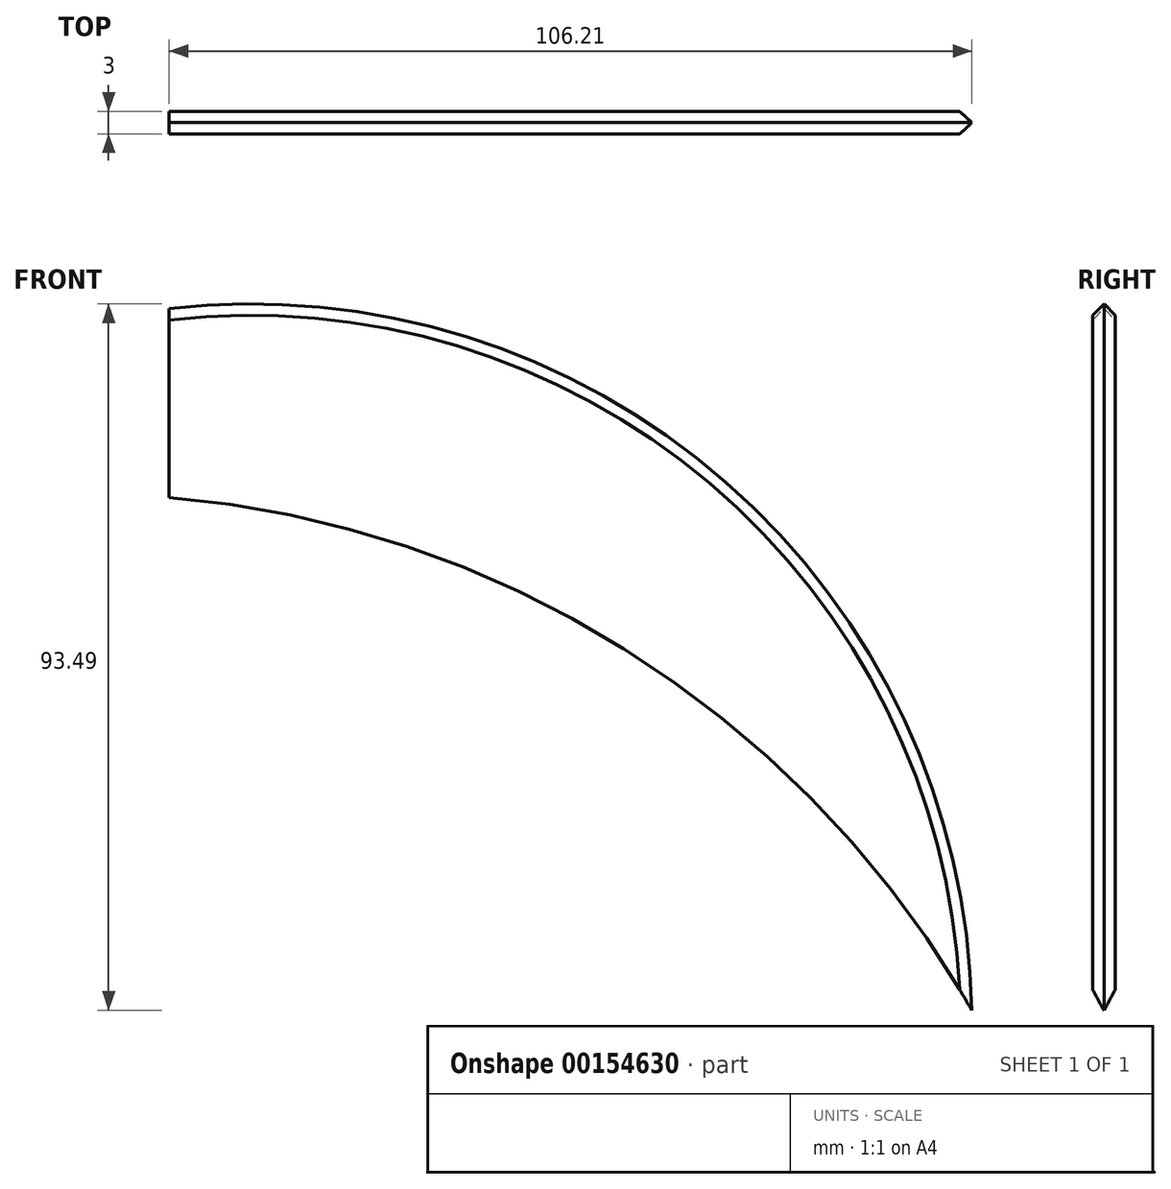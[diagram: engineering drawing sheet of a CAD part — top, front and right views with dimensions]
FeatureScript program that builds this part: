
annotation { "Feature Type Name" : "Feature", "Feature Type Description" : "" }
export const myFeature = defineFeature(function(context is Context, id is Id, definition is map)
    precondition{}
    {
        {
            var Q0;
            Q0=qCreatedBy(makeId("Front.planeOp"),FACE);
            var sketch = newSketch(context, id + "F0", { "sketchPlane" : qUnion([Q0])});
            skArc(sketch, "E0", {"start": v(106.2, -67.87) * mm, "mid": v(61.48, -20.83) * mm, "end": v(0, 0) * mm});
            skLineSegment(sketch, "E1", {"start": v(0, 0) * mm, "end": v(0, 25) * mm});
            skArc(sketch, "E2", {"start": v(106.2, -67.87) * mm, "mid": v(73.64, 2.05) * mm, "end": v(0, 25) * mm});
            skSolve(sketch);
        }
        {
            var Q0;
            Q0=makeQuery(id+"F0.imprint","IMPRINT",FACE,{"disambiguationData":[TD([[makeQuery(id+"F0.imprint","IMPRINT",EDGE,{"derivedFrom":sQuery(id+"F0.wireOp",EDGE,"E0")}),-1.0]])]});
            extrude(context, id + "F1", {"entities" : qUnion([Q0]), "depth" : 3 * mm});
        }
        {
            var Q0;
            Q0=makeQuery(id+"F1.opExtrude","CAP_EDGE",EDGE,{"disambiguationData":[OSD([sQuery(id+"F0.wireOp",EDGE,"E2")])],"isStart":false});
            var Q1;
            Q1=makeQuery(id+"F1.opExtrude","CAP_EDGE",EDGE,{"disambiguationData":[OSD([sQuery(id+"F0.wireOp",EDGE,"E2")])],"isStart":true});
            chamfer(context, id + "F2", {"entities" : qUnion([Q0, Q1]), "width" : 1.5 * mm, "tangentPropagation" : true});
        }
    });
